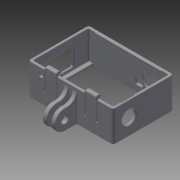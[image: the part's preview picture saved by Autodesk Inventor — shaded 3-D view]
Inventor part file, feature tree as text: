
AUTODESK INVENTOR PART (.ipt)
format: ipt  version: 2015 (Build 190159000, 159)  size: 643,584 bytes
history: native  units: mm
features: fillet x25, sketch x12, extrude x10, hole x5, mirror x2, plane x1
ambient origin geometry x8: Origin, YZ Plane, XZ Plane, XY Plane, X Axis, Y Axis, Z Axis, Center Point
bodies: Solid1 (feature_tree)
feature tree (55):
  sketch  "Sketch1"  dims[d0=60.0mm d1=41.5mm]
  extrude  "Extrusion1"  Depth=41.5mm
  extrude  "Extrusion2"  Depth=3.0mm
  extrude  "Extrusion3"  Depth=2.0mm TaperAngle=0.0deg
  plane  "Work Plane1"
  mirror  "Mirror1"
  extrude  "Extrusion4"  Depth=20.0mm
  extrude  "Extrusion5"  Depth=15.0mm
  mirror  "Mirror2"
  fillet  "Fillet5"  [1 undecoded]
  fillet  "Fillet6"  Radius=1.0mm
  fillet  "Fillet7"  Radius=8.0mm
  extrude  "Extrusion6"  Depth=23.5mm TaperAngle=0.0deg
  fillet  "Fillet8"  Radius=2.0mm
  sketch  "Sketch6"  dims[d19=1.0mm d20=23.5mm d21=0.0mm d22=2.0mm d23=0.0mm]
  hole  "Hole1"  [1 undecoded]
  fillet  "Fillet9"  Radius=2.0mm
  fillet  "Fillet10"  Radius=0.5mm
  hole  "Hole2"  [1 undecoded]
  fillet  "Fillet11"  Radius=50.0mm
  fillet  "Fillet12"  Radius=0.5mm
  extrude  "Extrusion7"  Depth=15.0mm
  fillet  "Fillet13"  Radius=12.5mm
  fillet  "Fillet14"  Radius=1.0mm
  hole  "Hole3"  [1 undecoded]
  fillet  "Fillet15"  Radius=7.5mm
  fillet  "Fillet16"  Radius=0.5mm
  extrude  "Extrusion8"  Depth=0.4mm
  fillet  "Fillet17"  Radius=24.2mm
  hole  "Hole4"  [1 undecoded]
  fillet  "Fillet18"  Radius=2.0mm
  extrude  "Extrusion9"  Depth=5.0mm
  fillet  "Fillet19"  Radius=4.0mm
  fillet  "Fillet20"  Radius=1.0mm
  fillet  "Fillet21"  Radius=1.0mm
  fillet  "Fillet22"  Radius=0.5mm
  fillet  "Fillet24"  Radius=12.0mm
  fillet  "Fillet25"  Radius=12.0mm
  extrude  "Extrusion10"  Depth=1.0mm
  fillet  "Fillet26"  Radius=0.5mm
  fillet  "Fillet27"  Radius=0.5mm
  fillet  "Fillet28"  Radius=0.5mm
  hole  "Hole5"  [1 undecoded]
  fillet  "Fillet29"  Radius=9.5mm
  fillet  "Fillet30"  Radius=0.5mm
  sketch  "Sketch2"  dims[d2=2.0mm d3=3.0mm]
  sketch  "Sketch3"  dims[d4=3.0mm d5=2.0mm d6=0.0mm]
  sketch  "Sketch4"  dims[d7=23.5mm d8=0.0mm d13=20.0mm]
  sketch  "Sketch5"  dims[d14=20.0mm d15=15.0mm d16=90.0deg d17=1.0mm d18=8.0mm]
  sketch  "Sketch7"  dims[d24=2.0mm d25=0.0mm d30=1.0mm d31=2.0mm d32=0.5mm]
  sketch  "Sketch8"  dims[d34=25.0mm d36=1.0mm d37=50.0mm d38=0.5mm d39=0.0mm]
  sketch  "Sketch9"  dims[d40=0.5mm d41=15.0mm d42=12.5mm]
  sketch  "Sketch10"  dims[d43=13.5mm d44=6.0mm d45=4.0mm d46=2.0mm d47=90.0deg d48=2.0mm d49=20.594885mm d50=1.0mm]
  sketch  "Sketch11"  dims[d51=0.5mm d52=7.0mm d53=7.5mm]
  sketch  "Sketch13"  dims[d54=2.5mm d55=6.0mm d56=4.0mm d57=2.0mm d58=90.0deg d59=2.0mm d60=20.594885mm d61=0.5mm d62=0.4mm d64=24.2mm d65=2.5mm d66=2.0mm d67=5.0mm d68=4.0mm d69=1.0mm d70=0.0mm d71=1.0mm d72=0.5mm d73=12.0mm d74=12.0mm d75=10.0mm d76=6.0mm d77=4.0mm d78=2.0mm d79=90.0deg d80=2.0mm d81=20.594885mm d82=1.0mm d83=0.5mm d84=0.5mm d85=0.0mm d86=0.5mm d87=5.0mm d88=9.5mm d89=3.0mm d90=6.0mm d91=4.0mm d92=2.0mm d93=90.0deg d94=2.0mm d95=20.594885mm d96=0.5mm d97=4.0mm d98=7.0mm d99=13.0mm d100=25.0mm d101=2.0mm d102=0.0mm d103=1.0mm d104=1.0mm d105=1.0mm d106=2.0mm d108=0.5mm d109=0.5mm d115=3.0mm d116=3.0mm d117=15.0mm d118=16.5mm d119=0.0mm d120=7.5mm d121=7.0mm d122=0.5mm d123=5.5mm d124=5.5mm d125=6.0mm d126=4.0mm d127=2.0mm d128=90.0deg d129=8.0mm d130=20.594885mm d131=0.5mm d132=0.5mm]
note: 6 required parameter values undecoded (feature->parameter linkage not recoverable at this tier; creation-order binding heuristic only, values carry confidence <= 0.55)
